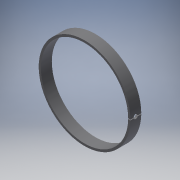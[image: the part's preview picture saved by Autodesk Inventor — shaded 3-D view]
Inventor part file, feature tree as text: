
AUTODESK INVENTOR PART (.ipt)
format: ipt  version: 2018 (Build 220112000, 112)  size: 146,944 bytes
history: native  units: mm
features: sketch x2, revolve x1, extrude x1, other x1
ambient origin geometry x8: Origin, YZ Plane, XZ Plane, XY Plane, X Axis, Y Axis, Z Axis, Center Point
bodies: Solid1 (feature_tree)
feature tree (5):
  revolve  "Revolution1"  [1 undecoded]
  extrude  "Extrusion1"  Depth=10.0mm
  sketch  "Sketch1"  dims[d0=5.0mm d1=200.0mm]
  sketch  "Sketch2"  dims[d2=25.0mm d3=62.65732mm d4=10.0mm d5=210.0mm d6=25.0mm d7=12.5mm d8=105.0mm d9=10.0mm d10=0.0mm]
  other  "Definition1"
note: 1 required parameter value undecoded (feature->parameter linkage not recoverable at this tier; creation-order binding heuristic only, values carry confidence <= 0.55)
